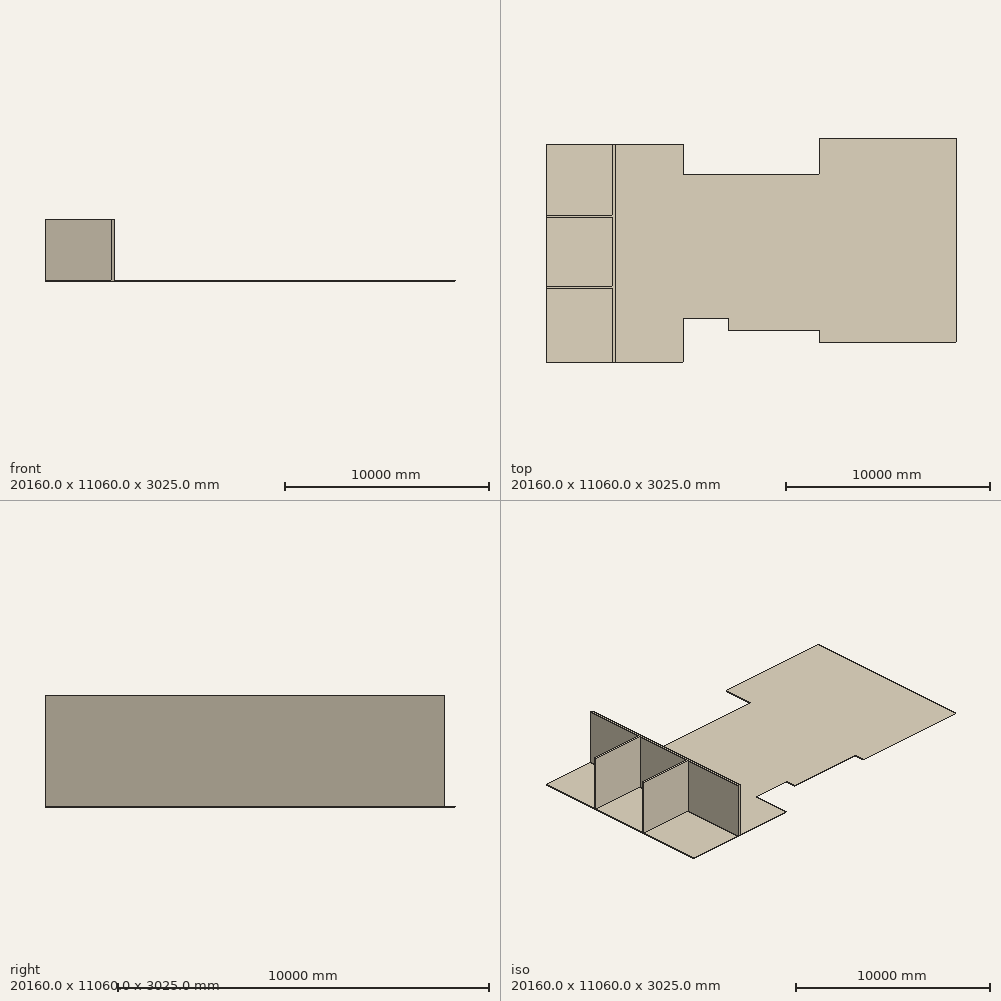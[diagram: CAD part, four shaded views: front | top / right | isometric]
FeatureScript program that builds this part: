
annotation { "Feature Type Name" : "Feature", "Feature Type Description" : "" }
export const myFeature = defineFeature(function(context is Context, id is Id, definition is map)
    precondition{}
    {
        {
            var Q0;
            Q0=qCreatedBy(makeId("Top.planeOp"),FACE);
            var sketch = newSketch(context, id + "F0", { "sketchPlane" : qUnion([Q0])});
            skLineSegment(sketch, "E0.bottom", {"start": v(-6760, 10060) * mm, "end": v(0, 10060) * mm});
            skLineSegment(sketch, "E0.top", {"start": v(-6760, 0) * mm, "end": v(0, 0) * mm});
            skLineSegment(sketch, "E0.left", {"start": v(-6760, 10060) * mm, "end": v(-6760, 8260) * mm});
            skLineSegment(sketch, "E0.right", {"start": v(0, 10060) * mm, "end": v(0, 0) * mm});
            skLineSegment(sketch, "E1.bottom", {"start": v(-13400, 8260) * mm, "end": v(-6760, 8260) * mm});
            skLineSegment(sketch, "E1.top", {"start": v(-13400, 1200) * mm, "end": v(-11200, 1200) * mm});
            skLineSegment(sketch, "E2.bottom", {"start": v(-13400, 9760) * mm, "end": v(-20160, 9760) * mm});
            skLineSegment(sketch, "E2.top", {"start": v(-13400, -1000) * mm, "end": v(-20160, -1000) * mm});
            skLineSegment(sketch, "E2.left", {"start": v(-13400, 9760) * mm, "end": v(-13400, 8260) * mm});
            skLineSegment(sketch, "E2.right", {"start": v(-20160, 9760) * mm, "end": v(-20160, -1000) * mm});
            skLineSegment(sketch, "E3.bottom", {"start": v(-6760, 600) * mm, "end": v(-11200, 600) * mm});
            skLineSegment(sketch, "E3.right", {"start": v(-11200, 600) * mm, "end": v(-11200, 1200) * mm});
            skLineSegment(sketch, "E4.trimOffspring", {"start": v(-6760, 600) * mm, "end": v(-6760, 0) * mm});
            skLineSegment(sketch, "E5.trimOffspring", {"start": v(-13400, 1200) * mm, "end": v(-13400, -1000) * mm});
            skSolve(sketch);
        }
        {
            var Q0;
            Q0 = qSketchRegion(id + "F0", true);
            extrude(context, id + "F1", {"entities" : qUnion([Q0]), "depth" : 25 * mm, "offsetDistance" : 25 * mm});
        }
        {
            var Q0;
            Q0=makeQuery(id+"F1.opExtrude","CAP_FACE",FACE,{"disambiguationData":[OSD([sQuery(id+"F0.wireOp",EDGE,"E0.bottom"),sQuery(id+"F0.wireOp",EDGE,"E0.top"),sQuery(id+"F0.wireOp",EDGE,"E0.left"),sQuery(id+"F0.wireOp",EDGE,"E0.right"),sQuery(id+"F0.wireOp",EDGE,"E1.bottom"),sQuery(id+"F0.wireOp",EDGE,"E1.top"),sQuery(id+"F0.wireOp",EDGE,"E2.bottom"),sQuery(id+"F0.wireOp",EDGE,"E2.top"),sQuery(id+"F0.wireOp",EDGE,"E2.left"),sQuery(id+"F0.wireOp",EDGE,"E2.right"),sQuery(id+"F0.wireOp",EDGE,"E3.bottom"),sQuery(id+"F0.wireOp",EDGE,"E3.right"),sQuery(id+"F0.wireOp",EDGE,"E4.trimOffspring"),sQuery(id+"F0.wireOp",EDGE,"E5.trimOffspring")])],"isStart":false});
            var sketch = newSketch(context, id + "F2", { "sketchPlane" : qUnion([Q0])});
            skLineSegment(sketch, "E6.bottom", {"start": v(-16930, 9760) * mm, "end": v(-16780, 9760) * mm});
            skLineSegment(sketch, "E6.top", {"start": v(-16930, -1000) * mm, "end": v(-16780, -1000) * mm});
            skLineSegment(sketch, "E6.left", {"start": v(-16930, 9760) * mm, "end": v(-16930, 1907.1) * mm});
            skLineSegment(sketch, "E6.right", {"start": v(-16780, 9760) * mm, "end": v(-16780, -1000) * mm});
            skLineSegment(sketch, "E7.bottom", {"start": v(-20160, 6160) * mm, "end": v(-16930, 6160) * mm});
            skLineSegment(sketch, "E7.top", {"start": v(-20160, 6260) * mm, "end": v(-16930, 6260) * mm});
            skLineSegment(sketch, "E7.left", {"start": v(-20160, 6160) * mm, "end": v(-20160, 6260) * mm});
            skLineSegment(sketch, "E7.right", {"start": v(-16930, 6160) * mm, "end": v(-16930, 6260) * mm});
            skLineSegment(sketch, "E8.bottom", {"start": v(-20160, 2760) * mm, "end": v(-16930, 2760) * mm});
            skLineSegment(sketch, "E8.right", {"start": v(-16930, 4380) * mm, "end": v(-16930, 2760) * mm});
            skLineSegment(sketch, "E9.trimOffspring", {"start": v(-16930, 2042.1) * mm, "end": v(-16930, -1000) * mm});
            skLineSegment(sketch, "E10", {"start": v(-20160, 2760) * mm, "end": v(-20160, 2660) * mm});
            skLineSegment(sketch, "E11", {"start": v(-20160, 2660) * mm, "end": v(-16930, 2660) * mm});
            skSolve(sketch);
        }
        {
            var Q0;
            Q0 = qSketchRegion(id + "F2", true);
            extrude(context, id + "F3", {"entities" : qUnion([Q0]), "operationType" : NewBodyOperationType.ADD, "depth" : 3000 * mm, "offsetDistance" : 25 * mm});
        }
    });
